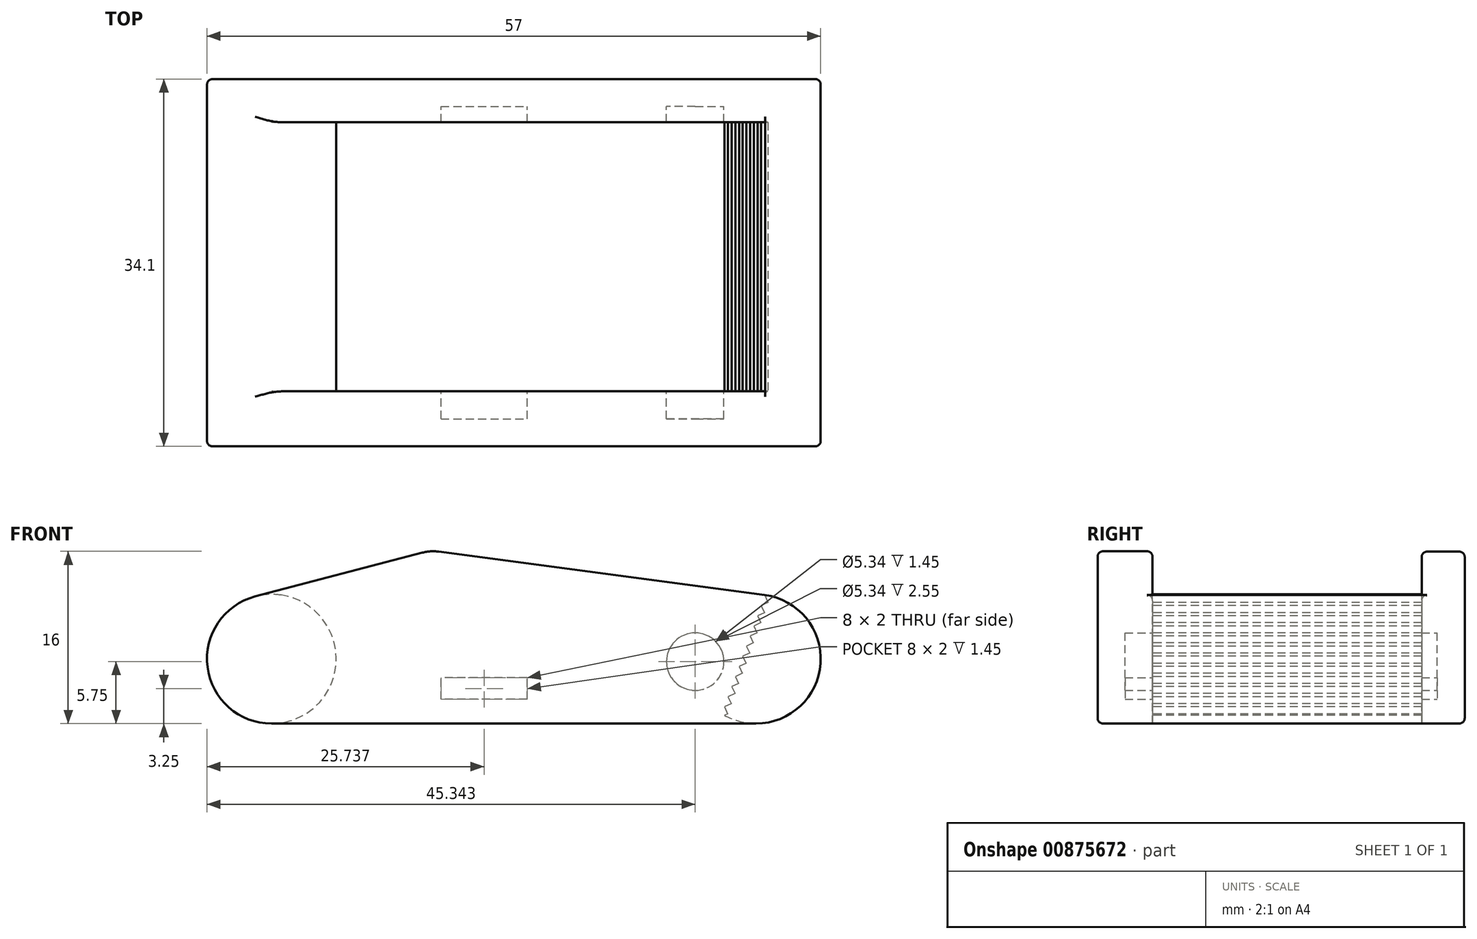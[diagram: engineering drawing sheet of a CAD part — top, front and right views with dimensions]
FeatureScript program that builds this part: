
annotation { "Feature Type Name" : "Feature", "Feature Type Description" : "" }
export const myFeature = defineFeature(function(context is Context, id is Id, definition is map)
    precondition{}
    {
        {
            var Q0;
            Q0=qCreatedBy(makeId("Front.planeOp"),FACE);
            var sketch = newSketch(context, id + "F0", { "sketchPlane" : qUnion([Q0])});
            skLineSegment(sketch, "E0", {"start": v(0.79, 5.95) * mm, "end": v(-29.47, 9.97) * mm});
            skLineSegment(sketch, "E1", {"start": v(-31.01, 9.87) * mm, "end": v(-46.52, 5.8) * mm});
            skLineSegment(sketch, "E2", {"start": v(0, -6) * mm, "end": v(-45, -6) * mm});
            skArc(sketch, "E3", {"start": v(0, -6) * mm, "mid": v(5.99, -0.4) * mm, "end": v(0.79, 5.95) * mm});
            skArc(sketch, "E4", {"start": v(-46.52, 5.8) * mm, "mid": v(-50.95, -0.77) * mm, "end": v(-45, -6) * mm});
            skArc(sketch, "E5.filletArc", {"start": v(-29.47, 9.97) * mm, "mid": v(-30.25, 10) * mm, "end": v(-31.01, 9.87) * mm});
            skSolve(sketch);
        }
        {
            var Q0;
            Q0=makeQuery(id+"F0.imprint","IMPRINT",FACE,{"disambiguationData":[TD([[makeQuery(id+"F0.imprint","IMPRINT",EDGE,{"derivedFrom":sQuery(id+"F0.wireOp",EDGE,"E0")}),1.0]])]});
            extrude(context, id + "F1", {"entities" : qUnion([Q0]), "oppositeDirection" : true, "depth" : 5.1 * mm, "offsetDistance" : 25 * mm});
        }
        {
            var Q0;
            Q0=makeQuery(id+"F1.opExtrude","CAP_FACE",FACE,{"disambiguationData":[OSD([sQuery(id+"F0.wireOp",EDGE,"E0"),sQuery(id+"F0.wireOp",EDGE,"E1"),sQuery(id+"F0.wireOp",EDGE,"E2"),sQuery(id+"F0.wireOp",EDGE,"E3"),sQuery(id+"F0.wireOp",EDGE,"E4"),sQuery(id+"F0.wireOp",EDGE,"E5.filletArc")])],"isStart":false});
            var sketch = newSketch(context, id + "F2", { "sketchPlane" : qUnion([Q0])});
            skCircle(sketch, "E6", {"center": v(45, 0) * mm, "radius": 6 * mm});
            skArc(sketch, "E7", {"start": v(-0.83, 5.94) * mm, "mid": v(-5.68, -1.92) * mm, "end": v(2.94, -5.23) * mm});
            skLineSegment(sketch, "E8", {"start": v(0, 0) * mm, "end": v(0, 9.41) * mm, "construction": true});
            skLineSegment(sketch, "E9", {"start": v(-1.24, 6.32) * mm, "end": v(3.7, -7.24) * mm, "construction": true});
            skLineSegment(sketch, "E10", {"start": v(-0.64, 5.42) * mm, "end": v(-1.11, 5.25) * mm, "construction": true});
            skLineSegment(sketch, "E11.0", {"start": v(-0.47, 4.95) * mm, "end": v(-0.94, 4.78) * mm, "construction": true});
            skLineSegment(sketch, "E12.0", {"start": v(-0.53, 4.4) * mm, "end": v(-0.77, 4.3) * mm});
            skLineSegment(sketch, "E13.0", {"start": v(0.04, 3.54) * mm, "end": v(-0.43, 3.37) * mm, "construction": true});
            skLineSegment(sketch, "E14.0", {"start": v(0.21, 3.07) * mm, "end": v(-0.26, 2.9) * mm, "construction": true});
            skLineSegment(sketch, "E15.0", {"start": v(0.38, 2.6) * mm, "end": v(-0.09, 2.43) * mm, "construction": true});
            skLineSegment(sketch, "E16.0", {"start": v(0.56, 2.13) * mm, "end": v(0.09, 1.96) * mm, "construction": true});
            skLineSegment(sketch, "E17.0", {"start": v(0.5, 1.57) * mm, "end": v(0.26, 1.49) * mm, "construction": true});
            skLineSegment(sketch, "E18.0", {"start": v(0.9, 1.19) * mm, "end": v(0.43, 1.02) * mm, "construction": true});
            skLineSegment(sketch, "E19.0", {"start": v(1.07, 0.72) * mm, "end": v(0.6, 0.55) * mm, "construction": true});
            skLineSegment(sketch, "E20.0", {"start": v(1.24, 0.25) * mm, "end": v(0.77, 0.08) * mm, "construction": true});
            skLineSegment(sketch, "E21.0", {"start": v(1.41, -0.22) * mm, "end": v(0.94, -0.4) * mm, "construction": true});
            skLineSegment(sketch, "E22.0", {"start": v(1.58, -0.7) * mm, "end": v(1.11, -0.86) * mm, "construction": true});
            skLineSegment(sketch, "E23.0", {"start": v(1.75, -1.16) * mm, "end": v(1.28, -1.33) * mm, "construction": true});
            skLineSegment(sketch, "E24.0", {"start": v(1.92, -1.63) * mm, "end": v(1.45, -1.8) * mm, "construction": true});
            skLineSegment(sketch, "E25.0", {"start": v(2.1, -2.1) * mm, "end": v(1.62, -2.27) * mm, "construction": true});
            skLineSegment(sketch, "E26.0", {"start": v(2.27, -2.57) * mm, "end": v(1.8, -2.74) * mm, "construction": true});
            skLineSegment(sketch, "E27.0", {"start": v(2.44, -3.04) * mm, "end": v(1.97, -3.21) * mm, "construction": true});
            skLineSegment(sketch, "E28.0", {"start": v(2.6, -3.51) * mm, "end": v(2.14, -3.68) * mm, "construction": true});
            skLineSegment(sketch, "E29.0", {"start": v(2.54, -4.07) * mm, "end": v(2.3, -4.15) * mm, "construction": true});
            skLineSegment(sketch, "E30.0", {"start": v(2.95, -4.45) * mm, "end": v(2.48, -4.62) * mm, "construction": true});
            skLineSegment(sketch, "E31.0", {"start": v(3.36, -4.83) * mm, "end": v(2.65, -5.1) * mm, "construction": true});
            skLineSegment(sketch, "E32.0", {"start": v(2.95, -4.45) * mm, "end": v(-0.83, 5.94) * mm, "construction": true});
            skLineSegment(sketch, "E33.0", {"start": v(-1.47, 6.24) * mm, "end": v(3.46, -7.32) * mm, "construction": true});
            skLineSegment(sketch, "E34.trimOffspring", {"start": v(-0.13, 4) * mm, "end": v(-0.6, 3.84) * mm, "construction": true});
            skLineSegment(sketch, "E35", {"start": v(-0.83, 5.94) * mm, "end": v(-1.11, 5.25) * mm});
            skLineSegment(sketch, "E36", {"start": v(-1.11, 5.25) * mm, "end": v(-0.47, 4.95) * mm});
            skLineSegment(sketch, "E37", {"start": v(-0.47, 4.95) * mm, "end": v(-0.77, 4.3) * mm});
            skLineSegment(sketch, "E38", {"start": v(-0.77, 4.3) * mm, "end": v(-0.13, 4) * mm});
            skLineSegment(sketch, "E39", {"start": v(-0.13, 4) * mm, "end": v(-0.43, 3.37) * mm});
            skLineSegment(sketch, "E40", {"start": v(-0.43, 3.37) * mm, "end": v(0.21, 3.07) * mm});
            skLineSegment(sketch, "E41", {"start": v(0.21, 3.07) * mm, "end": v(-0.09, 2.43) * mm});
            skLineSegment(sketch, "E42", {"start": v(-0.09, 2.43) * mm, "end": v(0.56, 2.13) * mm});
            skLineSegment(sketch, "E43", {"start": v(0.56, 2.13) * mm, "end": v(0.26, 1.49) * mm});
            skLineSegment(sketch, "E44", {"start": v(0.26, 1.49) * mm, "end": v(0.9, 1.19) * mm});
            skLineSegment(sketch, "E45", {"start": v(0.9, 1.19) * mm, "end": v(0.6, 0.55) * mm});
            skLineSegment(sketch, "E46", {"start": v(0.6, 0.55) * mm, "end": v(1.24, 0.25) * mm});
            skLineSegment(sketch, "E47", {"start": v(1.24, 0.25) * mm, "end": v(0.94, -0.4) * mm});
            skLineSegment(sketch, "E48", {"start": v(0.94, -0.4) * mm, "end": v(1.58, -0.7) * mm});
            skLineSegment(sketch, "E49", {"start": v(1.58, -0.7) * mm, "end": v(1.28, -1.33) * mm});
            skLineSegment(sketch, "E50", {"start": v(1.28, -1.33) * mm, "end": v(1.92, -1.63) * mm});
            skLineSegment(sketch, "E51", {"start": v(1.92, -1.63) * mm, "end": v(1.62, -2.27) * mm});
            skLineSegment(sketch, "E52", {"start": v(1.62, -2.27) * mm, "end": v(2.27, -2.57) * mm});
            skLineSegment(sketch, "E53", {"start": v(2.27, -2.57) * mm, "end": v(1.97, -3.21) * mm});
            skLineSegment(sketch, "E54", {"start": v(1.97, -3.21) * mm, "end": v(2.6, -3.51) * mm});
            skLineSegment(sketch, "E55", {"start": v(2.6, -3.51) * mm, "end": v(2.3, -4.15) * mm});
            skLineSegment(sketch, "E56", {"start": v(2.3, -4.15) * mm, "end": v(2.95, -4.45) * mm});
            skLineSegment(sketch, "E57", {"start": v(2.95, -4.45) * mm, "end": v(2.65, -5.1) * mm});
            skLineSegment(sketch, "E58", {"start": v(2.65, -5.1) * mm, "end": v(2.94, -5.23) * mm});
            skSolve(sketch);
        }
        {
            var Q0;
            Q0 = qSketchRegion(id + "F2", true);
            extrude(context, id + "F3", {"entities" : qUnion([Q0]), "operationType" : NewBodyOperationType.ADD, "depth" : 25 * mm, "offsetDistance" : 25 * mm});
        }
        {
            var Q0;
            Q0=makeQuery(id+"F3.opExtrude","CAP_FACE",FACE,{"disambiguationData":[OSD([sQuery(id+"F2.wireOp",EDGE,"E7")])],"isStart":false});
            var sketch = newSketch(context, id + "F4", { "sketchPlane" : qUnion([Q0])});
            skLineSegment(sketch, "E59", {"start": v(-0.79, 5.95) * mm, "end": v(29.08, 9.91) * mm});
            skLineSegment(sketch, "E60", {"start": v(31.4, 9.77) * mm, "end": v(46.52, 5.8) * mm});
            skLineSegment(sketch, "E61", {"start": v(0, -6) * mm, "end": v(45, -6) * mm});
            skArc(sketch, "E62.filletArc", {"start": v(-0.79, 5.95) * mm, "mid": v(-5.99, -0.4) * mm, "end": v(0, -6) * mm});
            skArc(sketch, "E63.filletArc", {"start": v(45, -6) * mm, "mid": v(50.95, -0.77) * mm, "end": v(46.52, 5.8) * mm});
            skArc(sketch, "E64.filletArc", {"start": v(31.4, 9.77) * mm, "mid": v(30.25, 9.95) * mm, "end": v(29.08, 9.91) * mm});
            skSolve(sketch);
        }
        {
            var Q0;
            Q0 = qSketchRegion(id + "F4", true);
            extrude(context, id + "F5", {"entities" : qUnion([Q0]), "operationType" : NewBodyOperationType.ADD, "depth" : 4 * mm, "offsetDistance" : 25 * mm});
        }
        {
            var Q0;
            Q0=qCreatedBy(makeId("Front.planeOp"),FACE);
            cPlane(context, id + "F6", {"entities" : qUnion([Q0]), "cplaneType" : CPlaneType.OFFSET, "offset" : 17.05 * mm, "oppositeDirection" : true, "width" : 150 * mm, "height" : 150 * mm});
        }
        {
            var Q0;
            Q0=qCreatedBy(id+"F6.planeOp",FACE);
            var sketch = newSketch(context, id + "F7", { "sketchPlane" : qUnion([Q0])});
            skCircle(sketch, "E65", {"center": v(-5.66, -0.25) * mm, "radius": 2.67 * mm});
            skLineSegment(sketch, "E66.bottom", {"start": v(-29.26, -1.75) * mm, "end": v(-21.26, -1.75) * mm});
            skLineSegment(sketch, "E66.top", {"start": v(-29.26, -3.75) * mm, "end": v(-21.26, -3.75) * mm});
            skLineSegment(sketch, "E66.left", {"start": v(-29.26, -1.75) * mm, "end": v(-29.26, -3.75) * mm});
            skLineSegment(sketch, "E66.right", {"start": v(-21.26, -1.75) * mm, "end": v(-21.26, -3.75) * mm});
            skSolve(sketch);
        }
        {
            var Q0;
            Q0 = qSketchRegion(id + "F7", true);
            extrude(context, id + "F8", {"entities" : qUnion([Q0]), "operationType" : NewBodyOperationType.REMOVE, "endBound" : BoundingType.SYMMETRIC, "depth" : 29 * mm, "offsetDistance" : 25 * mm});
        }
        {
            var Q0;
            Q0=makeQuery(id+"F1.opExtrude","CAP_EDGE",EDGE,{"disambiguationData":[OSD([sQuery(id+"F0.wireOp",EDGE,"E0")])],"isStart":false});
            var Q1;
            Q1=makeQuery(id+"F3.opExtrude","CAP_EDGE",EDGE,{"disambiguationData":[OSD([sQuery(id+"F2.wireOp",EDGE,"E6")])],"isStart":true});
            var Q2;
            Q2=makeQuery(id+"F3.opExtrude","CAP_EDGE",EDGE,{"disambiguationData":[OSD([sQuery(id+"F2.wireOp",EDGE,"E6")])],"isStart":false});
            var Q3;
            Q3=makeQuery(id+"F5.opExtrude","CAP_EDGE",EDGE,{"disambiguationData":[OSD([sQuery(id+"F4.wireOp",EDGE,"E60")])],"isStart":true});
            var Q4;
            Q4=makeQuery(id+"F5.opExtrude","CAP_EDGE",EDGE,{"disambiguationData":[OSD([sQuery(id+"F4.wireOp",EDGE,"E59")])],"isStart":false});
            var Q5;
            Q5=makeQuery(id+"F1.opExtrude","CAP_EDGE",EDGE,{"disambiguationData":[OSD([sQuery(id+"F0.wireOp",EDGE,"E0")])],"isStart":true});
            fillet(context, id + "F9", {"entities" : qUnion([Q0, Q1, Q2, Q3, Q4, Q5]), "radius" : .5 * mm, "tangentPropagation" : true, "allowEdgeOverflow" : false});
        }
    });
